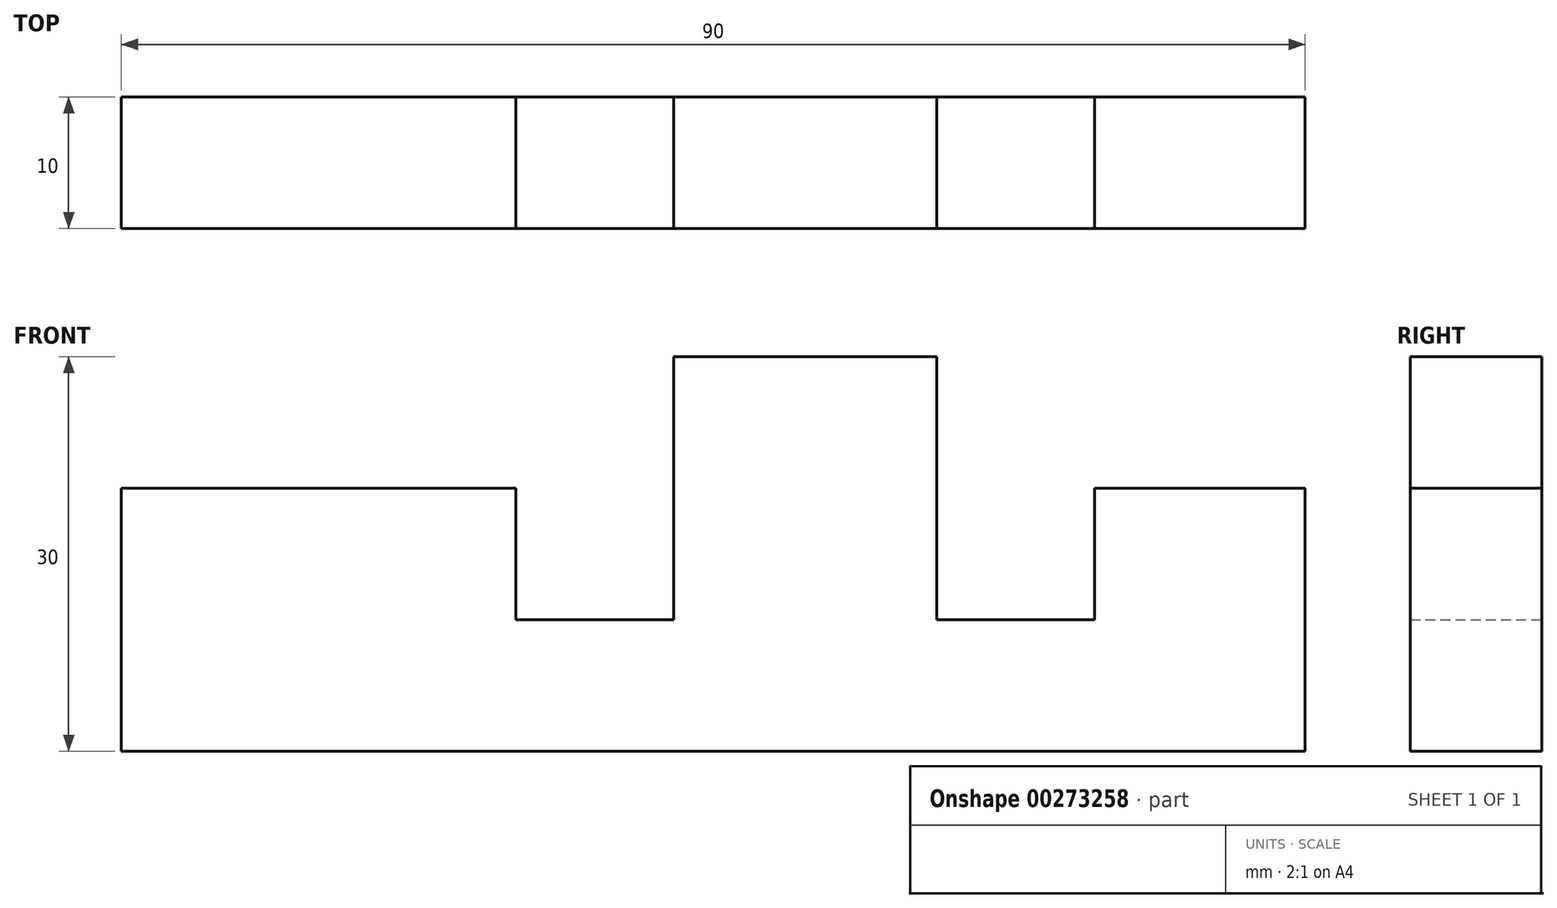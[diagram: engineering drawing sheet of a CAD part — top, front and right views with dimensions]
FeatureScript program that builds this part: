
annotation { "Feature Type Name" : "Feature", "Feature Type Description" : "" }
export const myFeature = defineFeature(function(context is Context, id is Id, definition is map)
    precondition{}
    {
        {
            var Q0;
            Q0=qCreatedBy(makeId("Front.planeOp"),FACE);
            var sketch = newSketch(context, id + "F0", { "sketchPlane" : qUnion([Q0])});
            skLineSegment(sketch, "E0", {"start": v(0, 0) * mm, "end": v(0, 20) * mm});
            skLineSegment(sketch, "E1", {"start": v(0, 20) * mm, "end": v(30, 20) * mm});
            skLineSegment(sketch, "E2", {"start": v(30, 20) * mm, "end": v(30, 10) * mm});
            skLineSegment(sketch, "E3", {"start": v(30, 10) * mm, "end": v(42, 10) * mm});
            skLineSegment(sketch, "E4", {"start": v(42, 10) * mm, "end": v(42, 30) * mm});
            skLineSegment(sketch, "E5", {"start": v(42, 30) * mm, "end": v(62, 30) * mm});
            skLineSegment(sketch, "E6", {"start": v(62, 30) * mm, "end": v(62, 10) * mm});
            skLineSegment(sketch, "E7", {"start": v(62, 10) * mm, "end": v(74, 10) * mm});
            skLineSegment(sketch, "E8", {"start": v(74, 10) * mm, "end": v(74, 20) * mm});
            skLineSegment(sketch, "E9", {"start": v(0, 0) * mm, "end": v(90, 0) * mm});
            skLineSegment(sketch, "E10", {"start": v(90, 0) * mm, "end": v(90, 20) * mm});
            skLineSegment(sketch, "E11", {"start": v(90, 20) * mm, "end": v(74, 20) * mm});
            skSolve(sketch);
        }
        {
            var Q0;
            Q0=makeQuery(id+"F0.imprint","IMPRINT",FACE,{"disambiguationData":[TD([[makeQuery(id+"F0.imprint","IMPRINT",EDGE,{"derivedFrom":sQuery(id+"F0.wireOp",EDGE,"E0")}),-1.0]])]});
            extrude(context, id + "F1", {"entities" : qUnion([Q0]), "depth" : 10 * mm});
        }
    });
